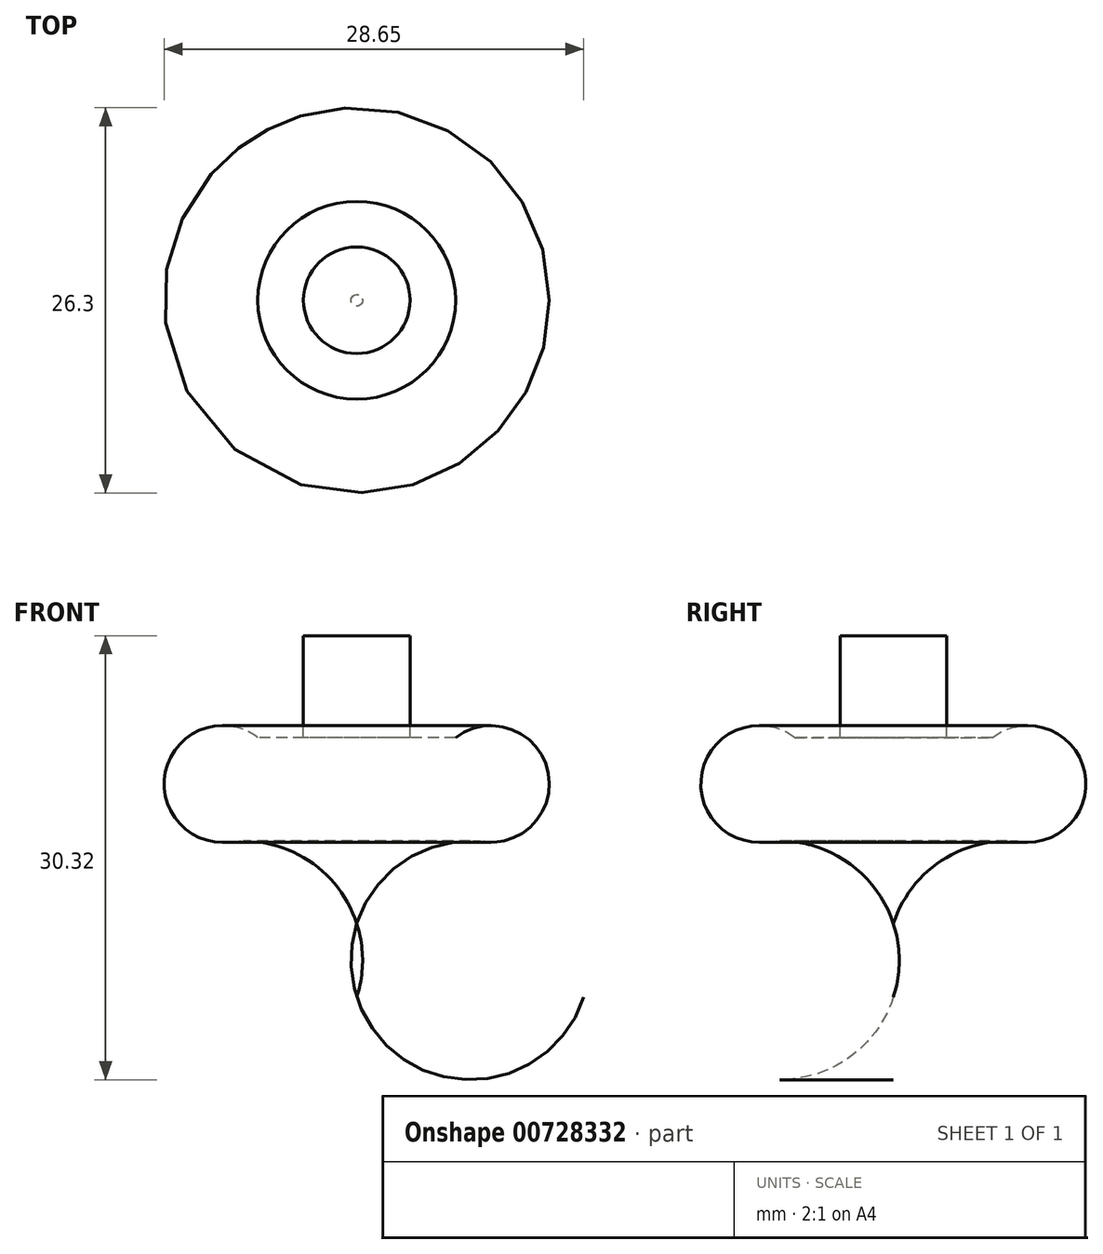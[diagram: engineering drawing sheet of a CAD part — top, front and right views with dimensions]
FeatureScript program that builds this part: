
annotation { "Feature Type Name" : "Feature", "Feature Type Description" : "" }
export const myFeature = defineFeature(function(context is Context, id is Id, definition is map)
    precondition{}
    {
        {
            var Q0;
            Q0=qCreatedBy(makeId("Front.planeOp"),FACE);
            var sketch = newSketch(context, id + "F0", { "sketchPlane" : qUnion([Q0])});
            skArc(sketch, "E0", {"start": v(8.7, 5.58) * mm, "mid": v(3.35, 4.35) * mm, "end": v(0, 0) * mm});
            skArc(sketch, "E1", {"start": v(8.7, 5.58) * mm, "mid": v(13.01, 10.59) * mm, "end": v(6.75, 12.7) * mm});
            skLineSegment(sketch, "E2", {"start": v(6.75, 12.7) * mm, "end": v(3.64, 12.7) * mm});
            skLineSegment(sketch, "E3", {"start": v(3.64, 12.7) * mm, "end": v(3.64, 19.66) * mm});
            skLineSegment(sketch, "E4", {"start": v(3.64, 19.66) * mm, "end": v(0, 19.66) * mm});
            skLineSegment(sketch, "E5", {"start": v(0, 19.66) * mm, "end": v(0, 0) * mm});
            skSolve(sketch);
        }
        {
            var Q0;
            Q0 = qSketchRegion(id + "F0", true);
            var Q1;
            Q1=sQuery(id+"F0.wireOp",EDGE,"E5");
            revolve(context, id + "F1", {"surfaceOperationType" : NewSurfaceOperationType.NEW, "entities" : qUnion([Q0]), "axis" : qUnion([Q1]), "revolveType" : RevolveType.FULL});
        }
        {
            var Q0;
            Q0=makeQuery(id+"F1.opRevolve","SWEPT_FACE",FACE,{"disambiguationData":[OSD([sQuery(id+"F0.wireOp",EDGE,"E4")])]});
            extrude(context, id + "F2", {"entities" : qUnion([Q0]), "operationType" : NewBodyOperationType.REMOVE, "depth" : 50.8 * mm, "offsetDistance" : 25.4 * mm});
        }
    });
